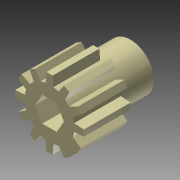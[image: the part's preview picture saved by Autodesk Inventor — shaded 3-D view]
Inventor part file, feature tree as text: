
AUTODESK INVENTOR PART (.ipt)
format: ipt  version: 2015 SP1 (Build 190203100, 203)  size: 222,208 bytes
history: native  units: in
note: dims shown in document units (in); Inventor stores cm internally (conversion verified against a paired STEP export)
features: extrude x4, sketch x4, projected_geometry x1
ambient origin geometry x8: Origin, YZ Plane, XZ Plane, XY Plane, X Axis, Y Axis, Z Axis, Center Point
bodies: Solid1 (feature_tree)
feature tree (9):
  extrude  "Extrusion1"  Depth=1.625in TaperAngle=0.0deg
  extrude  "Extrusion2"  Depth=0.9375in TaperAngle=0.0deg
  extrude  "Extrusion3"  Depth=0.5in
  extrude  "Extrusion4"  TaperAngle=120.0deg  [1 undecoded]
  sketch  "Sketch1"  dims[d0=0.9375in d1=1.625in d2=0.0in]
  sketch  "Sketch2"  dims[d3=1.0in d4=0.9375in d5=0.0in]
  sketch  "Sketch3"  dims[d6=0.5in d7=0.5in]
  sketch  "Sketch4"  dims[d8=0.5in d9=120.0deg d10=120.0deg d11=0.25in d12=0.25in d13=0.25in d14=2.0in d15=0.0in d16=0.5in d17=0.0in d18=0.1875in d19=90.0deg d20=0.5566in d21=0.6803in d22=0.0312in d23=0.0in d24=0.0625in d25=180.0deg d26=4.7244in d28=360.0deg d30=0.9375in d31=0.0in]
  projected_geometry  "Projected Loop1"
note: 1 required parameter value undecoded (feature->parameter linkage not recoverable at this tier; creation-order binding heuristic only, values carry confidence <= 0.55)
